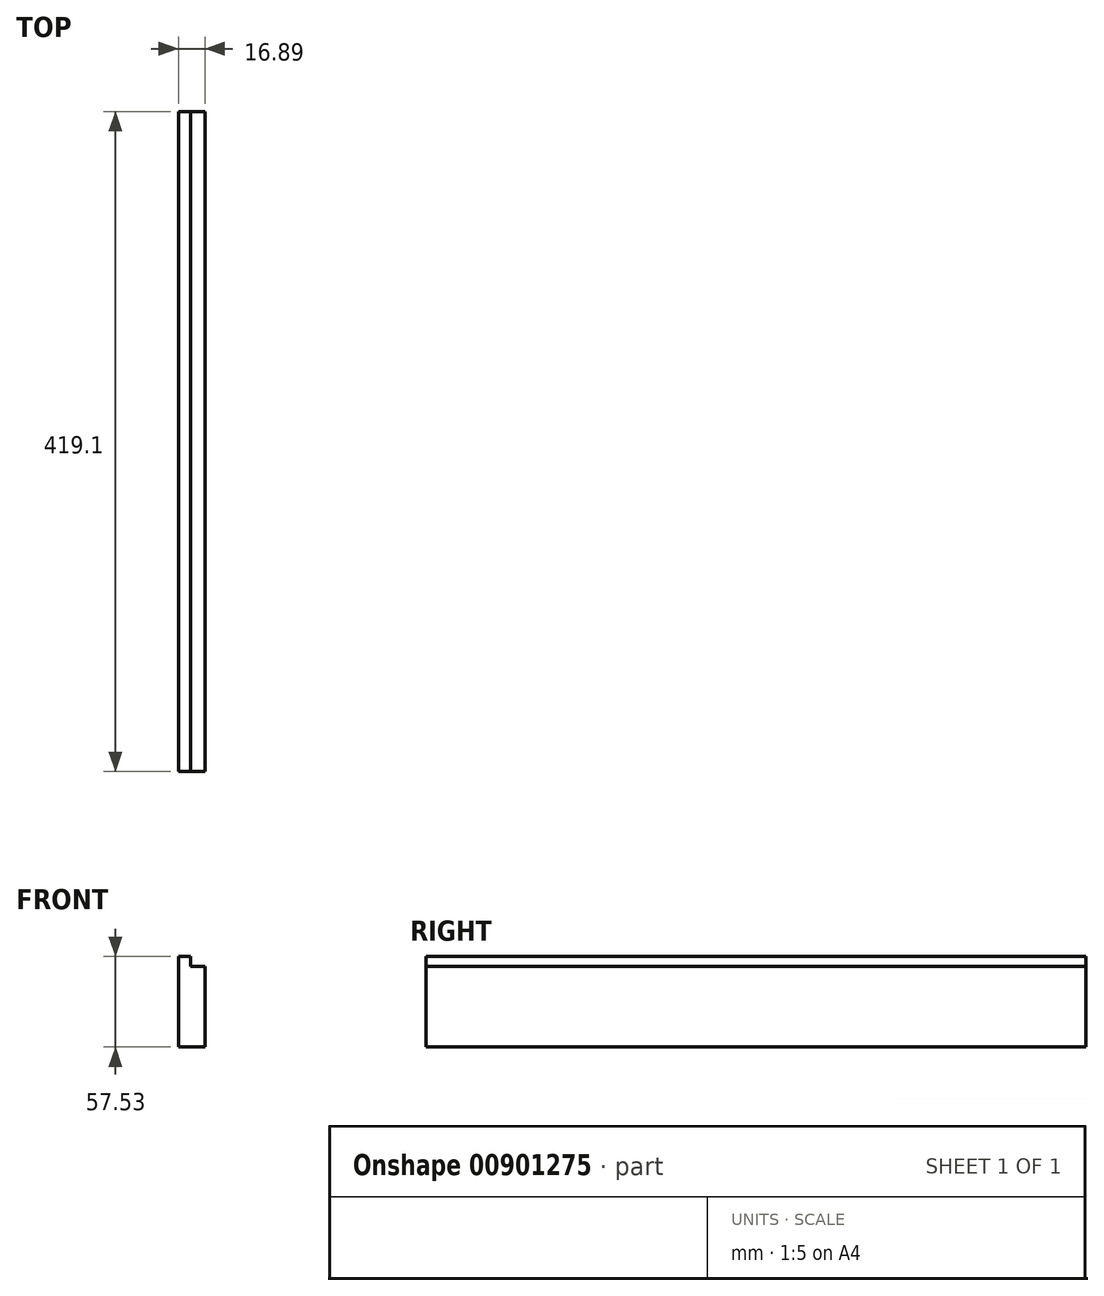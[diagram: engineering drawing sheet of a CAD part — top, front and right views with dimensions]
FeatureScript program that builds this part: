
annotation { "Feature Type Name" : "Feature", "Feature Type Description" : "" }
export const myFeature = defineFeature(function(context is Context, id is Id, definition is map)
    precondition{}
    {
        {
            var Q0;
            Q0=qCreatedBy(makeId("Right.planeOp"),FACE);
            var sketch = newSketch(context, id + "F0", { "sketchPlane" : qUnion([Q0])});
            skLineSegment(sketch, "E0.bottom", {"start": v(0, 0) * mm, "end": v(419.1, 0) * mm});
            skLineSegment(sketch, "E0.top", {"start": v(0, 51.18) * mm, "end": v(419.1, 51.18) * mm});
            skLineSegment(sketch, "E0.left", {"start": v(0, 0) * mm, "end": v(0, 51.18) * mm});
            skLineSegment(sketch, "E0.right", {"start": v(419.1, 0) * mm, "end": v(419.1, 51.18) * mm});
            skSolve(sketch);
        }
        {
            var Q0;
            Q0=qSketchRegion(id+"F0",true);
            extrude(context, id + "F1", {"entities" : qUnion([Q0]), "depth" : 16.9 * mm, "offsetDistance" : 25.4 * mm});
        }
        {
            var Q0;
            Q0=makeQuery(id+"F1.opExtrude","SWEPT_FACE",FACE,{"disambiguationData":[OSD([sQuery(id+"F0.wireOp",EDGE,"E0.top")])]});
            var sketch = newSketch(context, id + "F2", { "sketchPlane" : qUnion([Q0])});
            skLineSegment(sketch, "E1.bottom", {"start": v(0, 0) * mm, "end": v(7.75, 0) * mm});
            skLineSegment(sketch, "E1.top", {"start": v(0, 419.1) * mm, "end": v(7.75, 419.1) * mm});
            skLineSegment(sketch, "E1.left", {"start": v(0, 0) * mm, "end": v(0, 419.1) * mm});
            skLineSegment(sketch, "E1.right", {"start": v(7.75, 0) * mm, "end": v(7.75, 419.1) * mm});
            skSolve(sketch);
        }
        {
            var Q0;
            Q0=qSketchRegion(id+"F2",true);
            extrude(context, id + "F3", {"entities" : qUnion([Q0]), "operationType" : NewBodyOperationType.ADD, "depth" : 6.35 * mm, "offsetDistance" : 25.4 * mm});
        }
    });
